FCSTD DOCUMENT  (FreeCAD 0.16R6712 (Git))
Label: KNX_2Taster_Displayabdeckung
License: All rights reserved
LicenseURL: http://en.wikipedia.org/wiki/All_rights_reserved
objects: Sketcher::SketchObject×1
note: 1 computed .brp shape members not serialized (recipe doc carries the construction recipe); baked Part::Feature solids carry a one-line shape summary decoded from their .brp

FEATURE [Sketcher::SketchObject] Sketch
  sketch-geometry (18):
    g0: LineSegment StartX=2.69607 StartY=2.1171 StartZ=0 EndX=2.69607 EndY=38.3171 EndZ=0
    g1: LineSegment StartX=3.99607 StartY=39.6171 StartZ=0 EndX=57.8961 EndY=39.6171 EndZ=0
    g2: LineSegment StartX=59.1961 StartY=38.3171 StartZ=0 EndX=59.1961 EndY=2.1171 EndZ=0
    g3: LineSegment StartX=59.1961 StartY=2.1171 StartZ=0 EndX=2.69607 EndY=2.1171 EndZ=0
    g4: ArcOfCircle CenterX=3.99607 CenterY=38.3171 CenterZ=0 NormalX=0 NormalY=0 NormalZ=1 Radius=1.3 StartAngle=1.5708 EndAngle=3.14159
    g5: ArcOfCircle CenterX=57.8961 CenterY=38.3171 CenterZ=0 NormalX=0 NormalY=0 NormalZ=1 Radius=1.3 StartAngle=6.28319 EndAngle=7.85398
    g6: LineSegment StartX=8.44607 StartY=38.5171 StartZ=0 EndX=8.44607 EndY=3.5171 EndZ=0
    g7: LineSegment StartX=8.44607 StartY=3.5171 StartZ=0 EndX=24.9461 EndY=3.5171 EndZ=0
    g8: LineSegment StartX=24.9461 StartY=3.5171 StartZ=0 EndX=24.9461 EndY=3.2171 EndZ=0
    g9: LineSegment StartX=24.9461 StartY=3.2171 StartZ=0 EndX=36.9461 EndY=3.2171 EndZ=0
    g10: LineSegment StartX=36.9461 StartY=3.2171 StartZ=0 EndX=36.9461 EndY=3.5171 EndZ=0
    g11: LineSegment StartX=36.9461 StartY=3.5171 StartZ=0 EndX=53.4461 EndY=3.5171 EndZ=0
    g12: LineSegment StartX=53.4461 StartY=3.5171 StartZ=0 EndX=53.4461 EndY=38.5171 EndZ=0
    g13: LineSegment StartX=53.4461 StartY=38.5171 StartZ=0 EndX=8.44607 EndY=38.5171 EndZ=0
    g14: LineSegment StartX=10.7461 StartY=36.7171 StartZ=0 EndX=51.1461 EndY=36.7171 EndZ=0
    g15: LineSegment StartX=51.1461 StartY=36.7171 StartZ=0 EndX=51.1461 EndY=10.3171 EndZ=0
    g16: LineSegment StartX=51.1461 StartY=10.3171 StartZ=0 EndX=10.7461 EndY=10.3171 EndZ=0
    g17: LineSegment StartX=10.7461 StartY=10.3171 StartZ=0 EndX=10.7461 EndY=36.7171 EndZ=0
  constraints (54):
    c: Horizontal(g1)
    c: Vertical(g2)
    c: Coincident(g4,g1)
    c: Coincident(g4,g0)
    c: Coincident(g5,g1)
    c: Coincident(g5,g2)
    c: Tangent(g5,g1)
    c: Tangent(g2,g5)
    c: Tangent(g4,g1)
    c: DistanceX(g3,g3) = 56.5
    c: Equal(g0,g2)
    c: DistanceY(g2,g1) = 37.5
    c: Vertical(g6)
    c: Coincident(g7,g6)
    c: Horizontal(g7)
    c: Coincident(g8,g7)
    c: Coincident(g9,g8)
    c: Horizontal(g9)
    c: Horizontal(g11)
    c: Coincident(g12,g11)
    c: Vertical(g12)
    c: Coincident(g13,g12)
    c: Coincident(g13,g6)
    c: Horizontal(g13)
    c: DistanceX(g13,g13) = 45
    c: DistanceY(g12,g12) = 35
    c: Equal(g12,g6)
    c: Coincident(g10,g9)
    c: Coincident(g10,g11)
    c: Vertical(g10)
    c: Vertical(g8)
    c: DistanceX(g7,g7) = 16.5
    c: Equal(g7,g11)
    c: DistanceY(g10,g10) = 0.3
    c: DistanceX(g11,g2) = 5.75
    c: Coincident(g14,g15)
    c: Coincident(g15,g16)
    c: Coincident(g16,g17)
    c: Coincident(g17,g14)
    c: Horizontal(g14)
    c: Horizontal(g16)
    c: Vertical(g15)
    c: Vertical(g17)
    c: DistanceX(g14,g14) = 40.4
    c: DistanceY(g15,g15) = 26.4
    c: DistanceY(g14,g12) = 1.8
    c: DistanceX(g14,g12) = 2.3
    c: Horizontal(g3)
    c: Vertical(g0)
    c: Tangent(g4,g0)
    c: Coincident(g2,g3)
    c: Coincident(g0,g3)
    c: Radius(g4) = 1.3
    c: DistanceY(g12,g1) = 1.1
